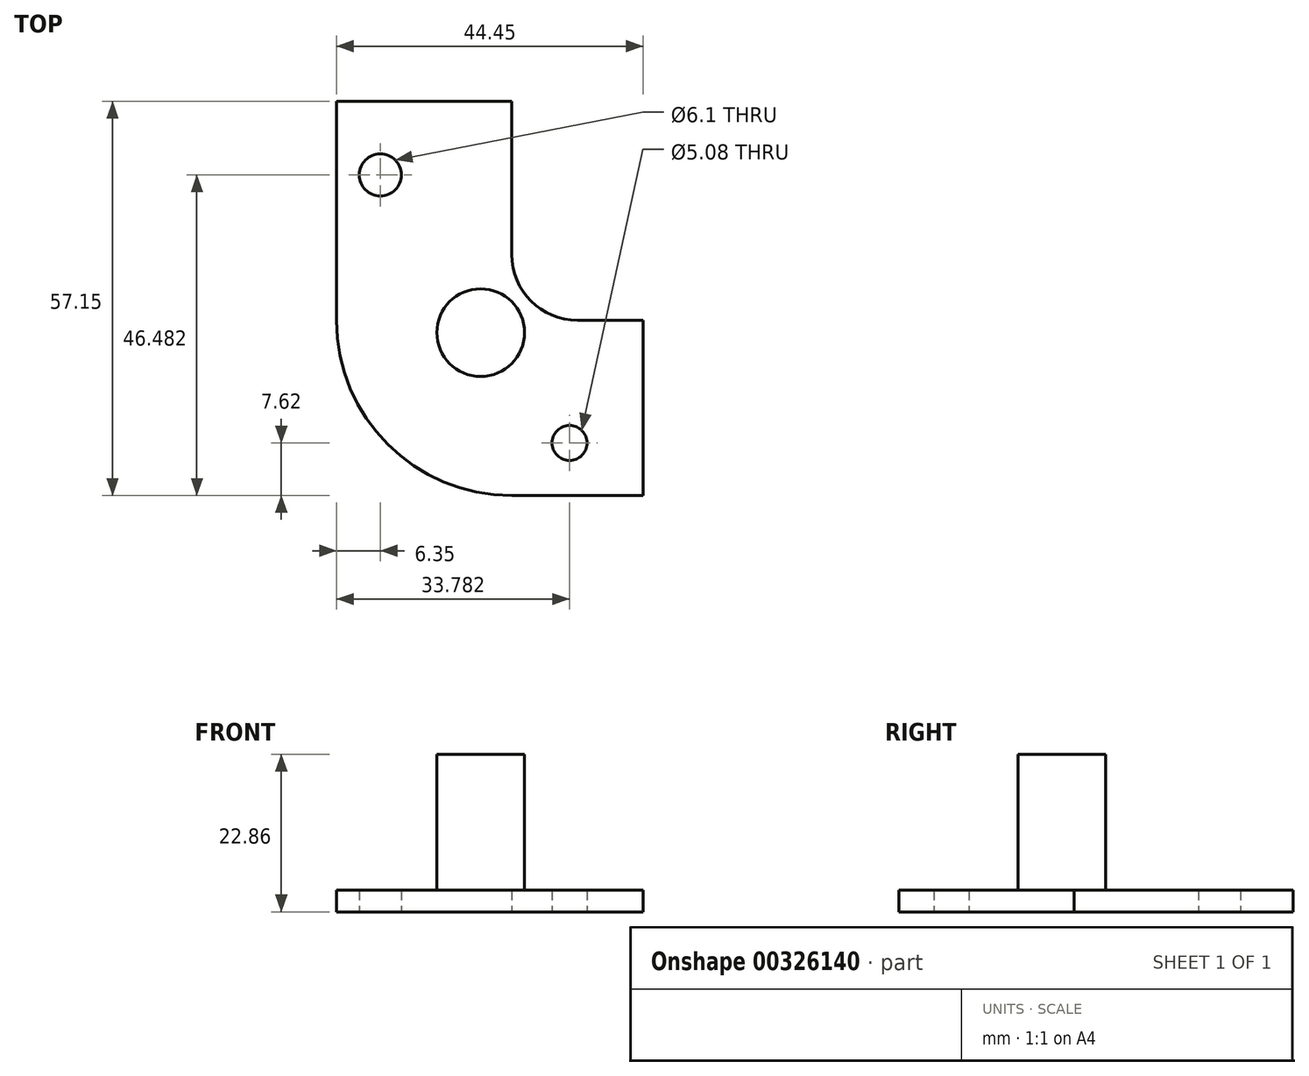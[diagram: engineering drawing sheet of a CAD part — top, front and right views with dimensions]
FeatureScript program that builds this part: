
annotation { "Feature Type Name" : "Feature", "Feature Type Description" : "" }
export const myFeature = defineFeature(function(context is Context, id is Id, definition is map)
    precondition{}
    {
        {
            var Q0;
            Q0=qCreatedBy(makeId("Top.planeOp"),FACE);
            var sketch = newSketch(context, id + "F0", { "sketchPlane" : qUnion([Q0])});
            skLineSegment(sketch, "E0", {"start": v(-25.4, 57.15) * mm, "end": v(-25.4, 25.4) * mm});
            skLineSegment(sketch, "E1", {"start": v(0, 0) * mm, "end": v(19.05, 0) * mm});
            skLineSegment(sketch, "E2", {"start": v(19.05, 0) * mm, "end": v(19.05, 25.4) * mm});
            skLineSegment(sketch, "E3", {"start": v(19.05, 25.4) * mm, "end": v(9.53, 25.4) * mm});
            skLineSegment(sketch, "E4", {"start": v(-25.4, 57.15) * mm, "end": v(0, 57.15) * mm});
            skLineSegment(sketch, "E5", {"start": v(0, 57.15) * mm, "end": v(0, 34.93) * mm});
            skPoint(sketch, "E6.visualSharp", {"position": v(0, 25.4) * mm});
            skArc(sketch, "E6.filletArc", {"start": v(0, 34.93) * mm, "mid": v(2.79, 28.19) * mm, "end": v(9.53, 25.4) * mm});
            skPoint(sketch, "E7.visualSharp", {"position": v(-25.4, 0) * mm});
            skArc(sketch, "E7.filletArc", {"start": v(-25.4, 25.4) * mm, "mid": v(-17.96, 7.44) * mm, "end": v(0, 0) * mm});
            skCircle(sketch, "E8", {"center": v(8.38, 7.62) * mm, "radius": 2.54 * mm});
            skCircle(sketch, "E9", {"center": v(-19.05, 46.48) * mm, "radius": 3.05 * mm});
            skCircle(sketch, "E10", {"center": v(-4.5, 23.62) * mm, "radius": 6.35 * mm});
            skSolve(sketch);
        }
        {
            var Q0;
            Q0=makeQuery(id+"F0.imprint","IMPRINT",FACE,{"disambiguationData":[TD([[makeQuery(id+"F0.imprint","IMPRINT",EDGE,{"derivedFrom":sQuery(id+"F0.wireOp",EDGE,"E10")}),1.0]])]});
            extrude(context, id + "F1", {"entities" : qUnion([Q0]), "depth" : 22.86 * mm});
        }
        {
            var Q0;
            Q0 = qSketchRegion(id + "F0", true);
            extrude(context, id + "F2", {"entities" : qUnion([Q0]), "operationType" : NewBodyOperationType.ADD, "depth" : 3.17 * mm});
        }
    });
